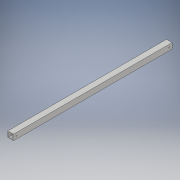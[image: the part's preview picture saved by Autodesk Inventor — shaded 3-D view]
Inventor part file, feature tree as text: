
AUTODESK INVENTOR PART (.ipt)
format: ipt  version: 2018 (Build 220112000, 112)  size: 113,152 bytes
history: native  units: in
note: dims shown in document units (in); Inventor stores cm internally (conversion verified against a paired STEP export)
features: extrude x2, sketch x2
ambient origin geometry x8: Origin, YZ Plane, XZ Plane, XY Plane, X Axis, Y Axis, Z Axis, Center Point
bodies: Solid1 (feature_tree)
feature tree (4):
  extrude  "Extrusion1"  Depth=1.0in
  extrude  "Extrusion2"  Depth=28.0in TaperAngle=0.0deg
  sketch  "Sketch1"  dims[d0=1.0in d1=1.0in]
  sketch  "Sketch2"  dims[d2=0.125in d3=28.0in d4=0.0in d5=0.5in d6=0.5in d7=0.2031in d8=1.0in d9=0.0in]
